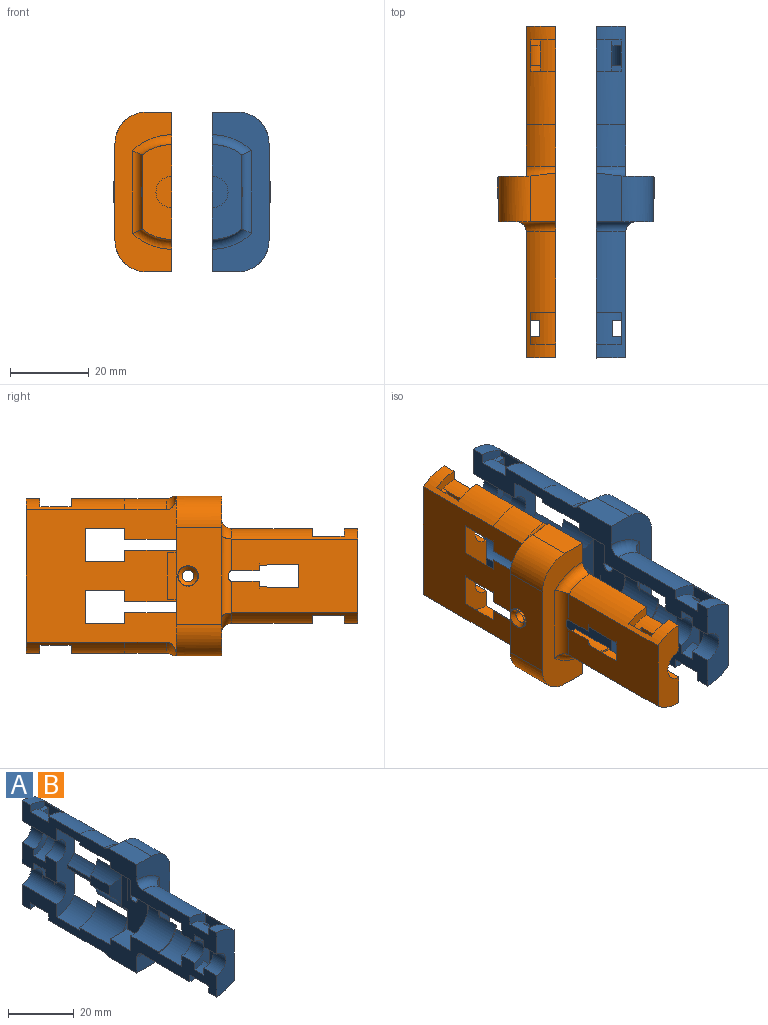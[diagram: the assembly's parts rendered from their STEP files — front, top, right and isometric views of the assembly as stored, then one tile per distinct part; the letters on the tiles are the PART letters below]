
ASSEMBLY  parts=2 mates=1
PART A: 101 faces, bbox 14.9x84x50.2 mm
  f0: cylinder r=12mm len=32mm, axis (0,1,0), area 204.3mm2, adj f26,f31,f46,f85,f95,f96,f98
  f1: cylinder r=12mm len=32mm, axis (0,1,0), area 204.3mm2, adj f25,f32,f46,f85,f89,f90,f98
  f2: cylinder r=11.64mm len=25mm, axis (0,-1,0), area 150mm2, adj f11,f31,f63,f64,f68,f79,f81,f99
  f3: cylinder r=11.64mm len=25mm, axis (0,-1,0), area 150mm2, adj f10,f32,f62,f63,f72,f75,f77,f99
  f4: cylinder r=8mm len=10mm, axis (0,1,0), area 97.2mm2, adj f15,f30,f31,f98
  f5: cylinder r=8mm len=10mm, axis (0,1,0), area 97.2mm2, adj f16,f30,f32,f98
  f6: cylinder r=8.63mm len=10mm, axis (0,-1,0), area 91.3mm2, adj f24,f29,f32,f99
  f7: cylinder r=8.63mm len=10mm, axis (0,-1,0), area 42.4mm2, adj f23,f29,f57,f99
  f8: cylinder r=8.63mm len=10mm, axis (0,-1,0), area 42.4mm2, adj f13,f29,f57,f99
  f9: cylinder r=8.63mm len=10mm, axis (0,-1,0), area 91.3mm2, adj f12,f29,f31,f99
  f10: plane 5.86x2.64mm, normal (0,1,0), area 0mm2, adj f3,f18,f99
  f11: plane 5.86x2.64mm, normal (0,1,0), area 0mm2, adj f2,f17,f99
  f12: plane 7.5x7.25mm, normal (0,1,0), area 9.5mm2, adj f9,f22,f31,f99
  f13: plane 5.88x2.88mm, normal (0,1,0), area 4.6mm2, adj f8,f21,f57,f99
  f14: cylinder r=7.62mm len=15.25mm, axis (0,-1,0), area 268.1mm2, adj f15,f16,f31,f32,f45,f47,f55,f98
  f15: plane 7.5x6.63mm, normal (0,-1,0), area 3.8mm2, adj f4,f14,f31,f98
  f16: plane 7.5x6.63mm, normal (0,-1,0), area 3.8mm2, adj f5,f14,f32,f98
  f17: cylinder r=11.62mm len=10.5mm, axis (0,-1,0), area 85.6mm2, adj f11,f27,f31,f64,f99
  f18: cylinder r=11.62mm len=10.5mm, axis (0,-1,0), area 85.6mm2, adj f10,f28,f32,f62,f99
  f19: cylinder r=7.62mm len=13mm, axis (0,-1,0), area 137.7mm2, adj f24,f32,f43,f54,f58,f99
  f20: cylinder r=7.62mm len=13mm, axis (0,-1,0), area 56mm2, adj f23,f43,f49,f57,f97,f99
  f21: cylinder r=7.62mm len=13mm, axis (0,-1,0), area 56mm2, adj f13,f43,f49,f57,f97,f99
  f22: cylinder r=7.62mm len=13mm, axis (0,-1,0), area 137.7mm2, adj f12,f31,f43,f44,f56,f99
  f23: plane 5.88x2.88mm, normal (0,1,0), area 4.6mm2, adj f7,f20,f57,f99
  f24: plane 7.5x7.25mm, normal (0,1,0), area 9.5mm2, adj f6,f19,f32,f99
  f25: torus R=14.5mm, axis (0,-1,0), area 36.5mm2, adj f1,f32,f59,f100
  f26: torus R=14.5mm, axis (0,-1,0), area 36.5mm2, adj f0,f31,f59,f100
  f27: torus R=14.12mm, axis (0,-1,0), area 23mm2, adj f17,f31,f43,f51,f60,f99
  f28: torus R=14.12mm, axis (0,-1,0), area 23mm2, adj f18,f32,f43,f53,f61,f99
  f29: plane 33.01x7.55mm, normal (0,-1,0), area 167.6mm2, adj f6,f7,f8,f9,f31,f32,f40,f41
  f30: plane 16.02x7.52mm, normal (0,1,0), area 73.6mm2, adj f4,f5,f31,f32,f35,f98
  f31: plane 84x16.25mm, normal (-1,0,0), area 444.9mm2, adj f0,f2,f4,f9,f12,f14,f15,f17
  f32: plane 84x16.25mm, normal (-1,0,0), area 444.9mm2, adj f1,f3,f5,f6,f14,f16,f18,f19
  f33: plane 17.23x6.5mm, normal (0,-1,0), area 62.7mm2, adj f31,f32,f35,f82,f83,f84,f85,f86
  f34: plane 17.23x6.5mm, normal (0,1,0), area 62.7mm2, adj f31,f32,f65,f82,f83,f84,f85,f86
  f35: cylinder r=4mm len=8mm, axis (0,1,0), area 69.1mm2, adj f30,f31,f32,f33
  f36: plane 14.71x6.47mm, normal (0,-1,0), area 40.7mm2, adj f41,f42,f66,f68,f69,f80
  f37: plane 14.71x6.47mm, normal (0,1,0), area 40.7mm2, adj f41,f42,f66,f68,f69,f78
  f38: plane 14.71x6.47mm, normal (0,-1,0), area 40.7mm2, adj f40,f41,f70,f71,f72,f76
  f39: plane 14.71x6.47mm, normal (0,1,0), area 40.7mm2, adj f40,f41,f70,f71,f72,f74
  f40: cylinder r=4mm len=15mm, axis (0,1,0), area 155.8mm2, adj f29,f32,f38,f39,f41,f63,f70
  f41: plane 15x7.75mm, normal (-1,0,0), area 91.2mm2, adj f29,f36,f37,f38,f39,f40,f42,f63
  f42: cylinder r=4mm len=15mm, axis (0,1,0), area 155.8mm2, adj f29,f31,f36,f37,f41,f63,f66
  f43: plane 40.47x7.54mm, normal (0,1,0), area 252.1mm2, adj f19,f20,f21,f22,f27,f28,f49,f52
  f44: plane 5.41x2.25mm, normal (0,1,0), area 8.4mm2, adj f22,f31,f50
  f45: plane 11.31x7.38mm, normal (0,1,0), area 52.4mm2, adj f14,f32,f48,f49
  f46: plane 24x7.5mm, normal (0,-1,0), area 142.3mm2, adj f0,f1,f31,f32,f65,f98
  f47: plane 11.31x7.38mm, normal (0,1,0), area 52.4mm2, adj f14,f31,f49,f50
  f48: plane 9x7.38mm, normal (0,0,-1), area 66.4mm2, adj f32,f45,f49,f54,f58
  f49: plane 26.5x11.25mm, normal (-1,0,0), area 258.2mm2, adj f20,f21,f43,f45,f47,f48,f50,f55
  f50: plane 9x7.38mm, normal (0,0,1), area 66.4mm2, adj f31,f44,f47,f49,f56
  f51: plane 12.22x6.38mm, normal (0,0,-1), area 75.8mm2, adj f27,f31,f59,f60
  f52: plane 24.5x11.5mm, normal (1,0,0), area 260.5mm2, adj f43,f59,f60,f61,f92
  f53: plane 12.21x6.38mm, normal (0,0,1), area 75.8mm2, adj f28,f32,f59,f61
  f54: plane 5.41x2.25mm, normal (0,1,0), area 8.4mm2, adj f19,f32,f48
  f55: plane 3.87x0.25mm, normal (0,-1,0), area 0.6mm2, adj f14,f49
  f56: plane 3.44x1.97mm, normal (0,-1,0), area 2.7mm2, adj f22,f49,f50
  f57: plane 18x3.63mm, normal (-1,0,0), area 41.3mm2, adj f7,f8,f13,f20,f21,f23,f29,f97
  f58: plane 3.44x1.97mm, normal (0,-1,0), area 2.7mm2, adj f19,f48,f49
  f59: plane 40.5x14.38mm, normal (0,-1,0), area 289.7mm2, adj f25,f26,f31,f32,f51,f52,f53,f60
  f60: cylinder r=8mm len=11.51mm, axis (0,-1,0), area 144.5mm2, adj f27,f43,f51,f52,f59
  f61: cylinder r=8mm len=11.51mm, axis (0,1,0), area 144.5mm2, adj f28,f43,f52,f53,f59
  f62: plane 1.64x0.12mm, normal (0,-1,0), area 0mm2, adj f3,f18,f32
  f63: plane 39.01x7.5mm, normal (0,1,0), area 229.7mm2, adj f2,f3,f31,f32,f40,f41,f42,f99
  f64: plane 1.64x0.12mm, normal (0,-1,0), area 0mm2, adj f2,f17,f31
  f65: cylinder r=4mm len=8mm, axis (0,1,0), area 69.1mm2, adj f31,f32,f34,f46
  f66: plane 8.13x5mm, normal (1,0,0), area 40.6mm2, adj f36,f37,f42,f67
  f67: cylinder r=9.14mm len=8mm, axis (0,-1,0), area 32.8mm2, adj f31,f66,f78,f79,f80,f81
  f68: plane 9.66x8.01mm, normal (-1,0,0.01), area 52.8mm2, adj f2,f36,f37,f69,f78,f79,f80,f81
  f69: cylinder r=6.5mm len=6.56mm, axis (0,-1,0), area 51.2mm2, adj f36,f37,f41,f68
  f70: plane 8.13x5mm, normal (1,0,0), area 40.6mm2, adj f38,f39,f40,f73
  f71: cylinder r=6.5mm len=6.56mm, axis (0,-1,0), area 51.2mm2, adj f38,f39,f41,f72
  f72: plane 9.66x8.01mm, normal (-1,0,-0.01), area 52.8mm2, adj f3,f38,f39,f71,f74,f75,f76,f77
  f73: cylinder r=9.14mm len=8mm, axis (0,-1,0), area 32.8mm2, adj f32,f70,f74,f75,f76,f77
  f74: plane 2.42x1.5mm, normal (0,0,1), area 3.6mm2, adj f39,f72,f73,f75
  f75: plane 6.39x3.43mm, normal (0,1,0), area 15.4mm2, adj f3,f32,f72,f73,f74
  f76: plane 2.42x1.5mm, normal (0,0,1), area 3.6mm2, adj f38,f72,f73,f77
  f77: plane 6.39x3.43mm, normal (0,-1,0), area 15.4mm2, adj f3,f32,f72,f73,f76
  f78: plane 2.42x1.5mm, normal (0,0,-1), area 3.6mm2, adj f37,f67,f68,f79
  f79: plane 6.39x3.43mm, normal (0,1,0), area 15.4mm2, adj f2,f31,f67,f68,f78
  f80: plane 2.42x1.5mm, normal (0,0,-1), area 3.6mm2, adj f36,f67,f68,f81
  f81: plane 6.39x3.43mm, normal (0,-1,0), area 15.4mm2, adj f2,f31,f67,f68,f80
  f82: cylinder r=6.5mm len=4mm, axis (0,-1,0), area 17.2mm2, adj f31,f33,f34,f83
  f83: plane 4x3.49mm, normal (1,0,0), area 14mm2, adj f33,f34,f82,f84
  f84: cylinder r=9.5mm len=8mm, axis (0,-1,0), area 45.1mm2, adj f31,f33,f34,f83,f85,f95,f96
  f85: plane 20.17x8mm, normal (-1,0,0), area 106mm2, adj f0,f1,f33,f34,f84,f86,f89,f90
  f86: cylinder r=9.5mm len=8mm, axis (0,-1,0), area 45.1mm2, adj f32,f33,f34,f85,f87,f89,f90
  f87: plane 4x3.49mm, normal (1,0,0), area 14mm2, adj f33,f34,f86,f88
  f88: cylinder r=6.5mm len=4mm, axis (0,-1,0), area 17.2mm2, adj f32,f33,f34,f87
  f89: plane 6.5x5.07mm, normal (0,1,0), area 17.5mm2, adj f1,f32,f85,f86
  f90: plane 6.5x5.07mm, normal (0,-1,0), area 17.5mm2, adj f1,f32,f85,f86
  f91: cylinder r=1.5mm len=6.5mm, axis (-1,0,0), area 61.3mm2, adj f49,f94
  f92: cylinder r=2.6mm len=5.2mm, axis (-1,0,0), area 8.2mm2, adj f52,f93
  f93: plane 5.2x5.2mm, normal (1,0,0), area 1.6mm2, adj f92,f94
  f94: cone r=1.5mm half-angle=45deg, axis (1,0,0), area 17.8mm2, adj f91,f93
  f95: plane 6.5x5.07mm, normal (0,1,0), area 17.5mm2, adj f0,f31,f84,f85
  f96: plane 6.5x5.07mm, normal (0,-1,0), area 17.5mm2, adj f0,f31,f84,f85
  f97: plane 11.88x2.75mm, normal (-0.71,-0.71,0), area 26.3mm2, adj f20,f21,f49,f57
  f98: plane 32x18.74mm, normal (1,0,0), area 524.8mm2, adj f0,f1,f4,f5,f14,f15,f16,f30
  f99: plane 39.69x38mm, normal (1,0,0), area 1036.6mm2, adj f2,f3,f6,f7,f8,f9,f10,f11
  f100: cylinder r=2.5mm len=21mm, axis (0,0,1), area 76.3mm2, adj f14,f25,f26,f59,f98
PART B: same geometry as A
PLACE A t=(0.97,-7.66,6.8)mm
PLACE B rot(axis=(0,1,0),180deg) t=(-9.28,-7.66,6.8)mm
MATE pin_slot B.f91 <-> A.f92  axis (1,0,0) through (-16.65,10.34,6.8)mm
